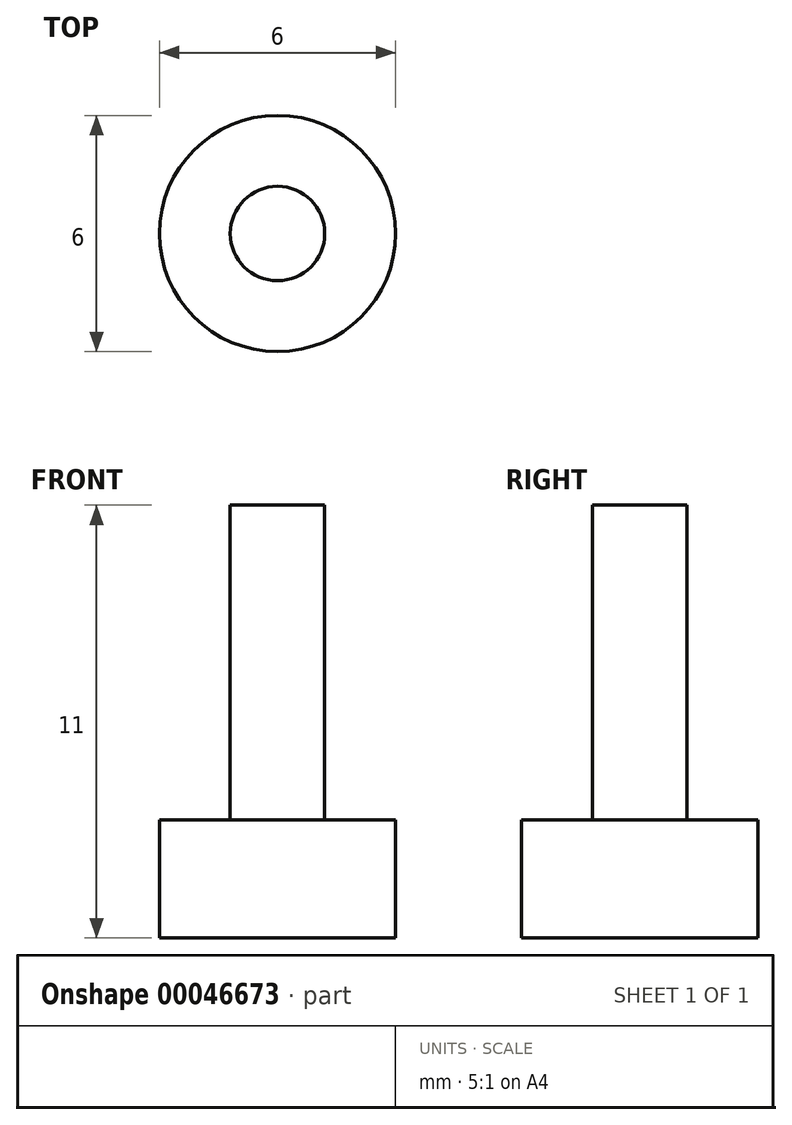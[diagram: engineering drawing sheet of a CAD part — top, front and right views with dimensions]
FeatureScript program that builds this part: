
annotation { "Feature Type Name" : "Feature", "Feature Type Description" : "" }
export const myFeature = defineFeature(function(context is Context, id is Id, definition is map)
    precondition{}
    {
        {
            var Q0;
            Q0=qCreatedBy(makeId("Top.planeOp"),FACE);
            var sketch = newSketch(context, id + "F0", { "sketchPlane" : qUnion([Q0])});
            skCircle(sketch, "E0", {"center": v(0, 0) * mm, "radius": 3 * mm});
            skSolve(sketch);
        }
        {
            var Q0;
            Q0=makeQuery(id+"F0.imprint","IMPRINT",FACE,{"disambiguationData":[TD([[makeQuery(id+"F0.imprint","IMPRINT",EDGE,{"derivedFrom":sQuery(id+"F0.wireOp",EDGE,"E0")}),1.0]])]});
            extrude(context, id + "F1", {"entities" : qUnion([Q0]), "depth" : 3 * mm});
        }
        {
            var Q0;
            Q0=makeQuery(id+"F1.opExtrude","CAP_FACE",FACE,{"disambiguationData":[OSD([sQuery(id+"F0.wireOp",EDGE,"E0")])],"isStart":false});
            var sketch = newSketch(context, id + "F2", { "sketchPlane" : qUnion([Q0])});
            skCircle(sketch, "E1.0", {"center": v(0, 0) * mm, "radius": 3 * mm});
            skCircle(sketch, "E2", {"center": v(0, 0) * mm, "radius": 1.2 * mm});
            skSolve(sketch);
        }
        {
            var Q0;
            Q0=makeQuery(id+"F2.imprint","IMPRINT",FACE,{"disambiguationData":[TD([[makeQuery(id+"F2.imprint","IMPRINT",EDGE,{"derivedFrom":sQuery(id+"F2.wireOp",EDGE,"E2")}),1.0]])]});
            extrude(context, id + "F3", {"entities" : qUnion([Q0]), "operationType" : NewBodyOperationType.ADD, "depth" : 8 * mm});
        }
    });
